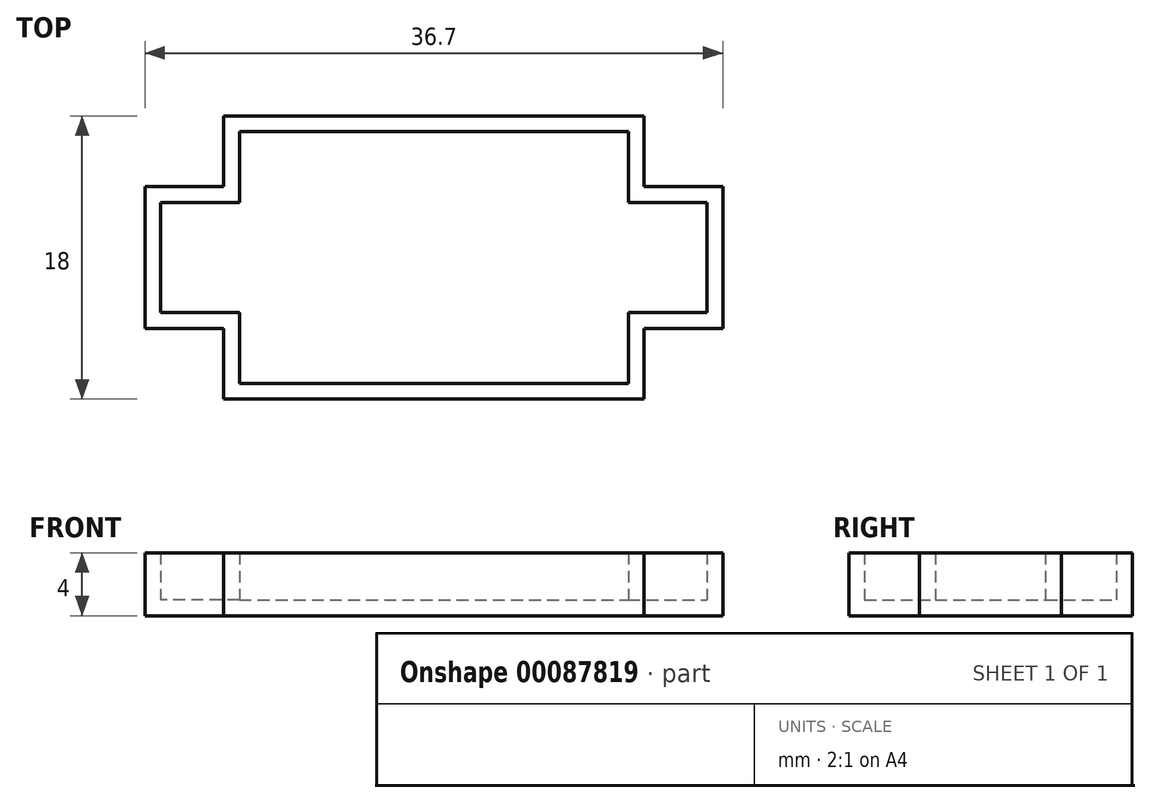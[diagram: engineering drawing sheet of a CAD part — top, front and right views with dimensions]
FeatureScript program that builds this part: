
annotation { "Feature Type Name" : "Feature", "Feature Type Description" : "" }
export const myFeature = defineFeature(function(context is Context, id is Id, definition is map)
    precondition{}
    {
        {
            var Q0;
            Q0=qCreatedBy(makeId("Top.planeOp"),FACE);
            var sketch = newSketch(context, id + "F0", { "sketchPlane" : qUnion([Q0])});
            skLineSegment(sketch, "E0.bottom", {"start": v(0, 0) * mm, "end": v(22.7, 0) * mm});
            skLineSegment(sketch, "E0.top", {"start": v(0, 14) * mm, "end": v(22.7, 14) * mm});
            skLineSegment(sketch, "E0.left", {"start": v(0, 0) * mm, "end": v(0, 4.5) * mm});
            skLineSegment(sketch, "E0.right", {"start": v(22.7, 0) * mm, "end": v(22.7, 4.5) * mm});
            skLineSegment(sketch, "E1.bottom", {"start": v(0, 4.5) * mm, "end": v(-5, 4.5) * mm});
            skLineSegment(sketch, "E1.top", {"start": v(0, 9.5) * mm, "end": v(-5, 9.5) * mm});
            skLineSegment(sketch, "E1.left", {"start": v(0, 4.5) * mm, "end": v(0, 9.5) * mm});
            skLineSegment(sketch, "E1.right", {"start": v(-5, 4.5) * mm, "end": v(-5, 9.5) * mm});
            skLineSegment(sketch, "E2.bottom", {"start": v(22.7, 4.5) * mm, "end": v(27.7, 4.5) * mm});
            skLineSegment(sketch, "E2.top", {"start": v(22.7, 9.5) * mm, "end": v(27.7, 9.5) * mm});
            skLineSegment(sketch, "E2.left", {"start": v(22.7, 4.5) * mm, "end": v(22.7, 9.5) * mm});
            skLineSegment(sketch, "E2.right", {"start": v(27.7, 4.5) * mm, "end": v(27.7, 9.5) * mm});
            skLineSegment(sketch, "E3", {"start": v(22.7, 9.5) * mm, "end": v(22.7, 14) * mm});
            skLineSegment(sketch, "E4", {"start": v(0, 9.5) * mm, "end": v(0, 14) * mm});
            skLineSegment(sketch, "E5.0", {"start": v(-2, 11.5) * mm, "end": v(-2, 16) * mm});
            skLineSegment(sketch, "E5.1", {"start": v(24.7, 2.5) * mm, "end": v(29.7, 2.5) * mm});
            skLineSegment(sketch, "E5.2", {"start": v(29.7, 2.5) * mm, "end": v(29.7, 11.5) * mm});
            skLineSegment(sketch, "E5.3", {"start": v(24.7, 11.5) * mm, "end": v(29.7, 11.5) * mm});
            skLineSegment(sketch, "E5.4", {"start": v(24.7, 11.5) * mm, "end": v(24.7, 16) * mm});
            skLineSegment(sketch, "E5.5", {"start": v(24.7, -2) * mm, "end": v(24.7, 2.5) * mm});
            skLineSegment(sketch, "E5.6", {"start": v(-2, 16) * mm, "end": v(24.7, 16) * mm});
            skLineSegment(sketch, "E5.7", {"start": v(-2, -2) * mm, "end": v(24.7, -2) * mm});
            skLineSegment(sketch, "E5.8", {"start": v(-2, -2) * mm, "end": v(-2, 2.5) * mm});
            skLineSegment(sketch, "E5.9", {"start": v(-2, 2.5) * mm, "end": v(-7, 2.5) * mm});
            skLineSegment(sketch, "E5.10", {"start": v(-7, 2.5) * mm, "end": v(-7, 11.5) * mm});
            skLineSegment(sketch, "E5.11", {"start": v(-2, 11.5) * mm, "end": v(-7, 11.5) * mm});
            skLineSegment(sketch, "E6.0", {"start": v(-1, 10.5) * mm, "end": v(-1, 15) * mm});
            skLineSegment(sketch, "E6.1", {"start": v(23.7, 3.5) * mm, "end": v(28.7, 3.5) * mm});
            skLineSegment(sketch, "E6.2", {"start": v(28.7, 3.5) * mm, "end": v(28.7, 10.5) * mm});
            skLineSegment(sketch, "E6.3", {"start": v(23.7, 10.5) * mm, "end": v(28.7, 10.5) * mm});
            skLineSegment(sketch, "E6.4", {"start": v(23.7, 10.5) * mm, "end": v(23.7, 15) * mm});
            skLineSegment(sketch, "E6.5", {"start": v(23.7, -1) * mm, "end": v(23.7, 3.5) * mm});
            skLineSegment(sketch, "E6.6", {"start": v(-1, 15) * mm, "end": v(23.7, 15) * mm});
            skLineSegment(sketch, "E6.7", {"start": v(-1, -1) * mm, "end": v(23.7, -1) * mm});
            skLineSegment(sketch, "E6.8", {"start": v(-1, -1) * mm, "end": v(-1, 3.5) * mm});
            skLineSegment(sketch, "E6.9", {"start": v(-1, 3.5) * mm, "end": v(-6, 3.5) * mm});
            skLineSegment(sketch, "E6.10", {"start": v(-6, 3.5) * mm, "end": v(-6, 10.5) * mm});
            skLineSegment(sketch, "E6.11", {"start": v(-1, 10.5) * mm, "end": v(-6, 10.5) * mm});
            skSolve(sketch);
        }
        {
            var Q0;
            Q0=makeQuery(id+"F0.imprint","IMPRINT",FACE,{"disambiguationData":[TD([[makeQuery(id+"F0.imprint","IMPRINT",EDGE,{"derivedFrom":sQuery(id+"F0.wireOp",EDGE,"E5.0")}),-1.0]])]});
            extrude(context, id + "F1", {"entities" : qUnion([Q0]), "depth" : 4 * mm});
        }
        {
            var Q0;
            Q0=makeQuery(id+"F0.imprint","IMPRINT",FACE,{"disambiguationData":[TD([[makeQuery(id+"F0.imprint","IMPRINT",EDGE,{"derivedFrom":sQuery(id+"F0.wireOp",EDGE,"E0.bottom")}),1.0]])]});
            var Q1;
            Q1=makeQuery(id+"F0.imprint","IMPRINT",FACE,{"disambiguationData":[TD([[makeQuery(id+"F0.imprint","IMPRINT",EDGE,{"derivedFrom":sQuery(id+"F0.wireOp",EDGE,"E1.bottom")}),-1.0]])]});
            var Q2;
            Q2=makeQuery(id+"F0.imprint","IMPRINT",FACE,{"disambiguationData":[TD([[makeQuery(id+"F0.imprint","IMPRINT",EDGE,{"derivedFrom":sQuery(id+"F0.wireOp",EDGE,"E2.bottom")}),1.0]])]});
            var Q3;
            Q3=makeQuery(id+"F0.imprint","IMPRINT",FACE,{"disambiguationData":[TD([[makeQuery(id+"F0.imprint","IMPRINT",EDGE,{"derivedFrom":sQuery(id+"F0.wireOp",EDGE,"E0.bottom")}),-1.0]])]});
            extrude(context, id + "F2", {"entities" : qUnion([Q0, Q1, Q2, Q3]), "operationType" : NewBodyOperationType.ADD, "depth" : 1 * mm});
        }
    });
